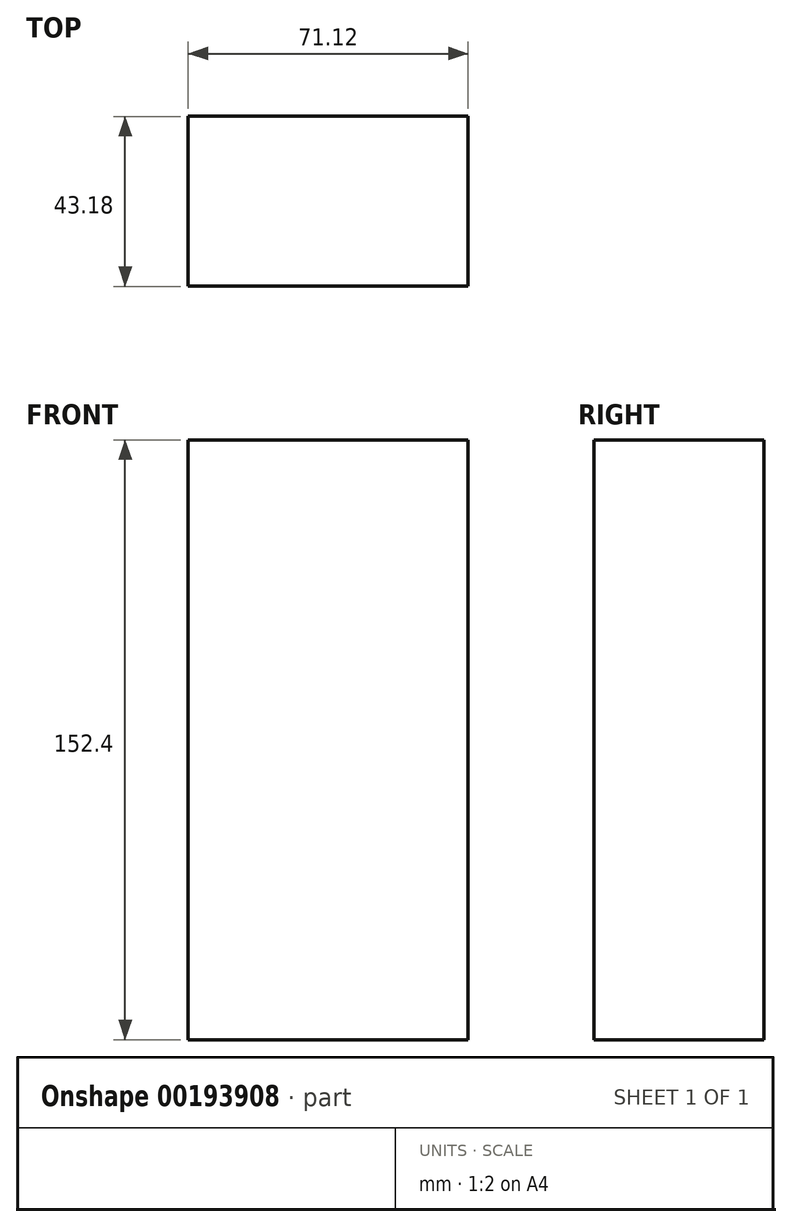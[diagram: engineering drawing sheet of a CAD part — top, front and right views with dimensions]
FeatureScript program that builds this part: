
annotation { "Feature Type Name" : "Feature", "Feature Type Description" : "" }
export const myFeature = defineFeature(function(context is Context, id is Id, definition is map)
    precondition{}
    {
        {
            var Q0;
            Q0=qCreatedBy(makeId("Top.planeOp"),FACE);
            var sketch = newSketch(context, id + "F0", { "sketchPlane" : qUnion([Q0])});
            skLineSegment(sketch, "E0.bottom", {"start": v(-42.83, 16.01) * mm, "end": v(28.3, 16.01) * mm});
            skLineSegment(sketch, "E0.top", {"start": v(-42.83, -27.17) * mm, "end": v(28.3, -27.17) * mm});
            skLineSegment(sketch, "E0.left", {"start": v(-42.83, 16.01) * mm, "end": v(-42.83, -27.17) * mm});
            skLineSegment(sketch, "E0.right", {"start": v(28.3, 16.01) * mm, "end": v(28.3, -27.17) * mm});
            skSolve(sketch);
        }
        {
            var Q0;
            Q0=makeQuery(id+"F0.imprint","IMPRINT",FACE,{"disambiguationData":[TD([[makeQuery(id+"F0.imprint","IMPRINT",EDGE,{"derivedFrom":sQuery(id+"F0.wireOp",EDGE,"E0.bottom")}),-1.0]])]});
            extrude(context, id + "F1", {"entities" : qUnion([Q0]), "depth" : 152.4 * mm});
        }
    });
